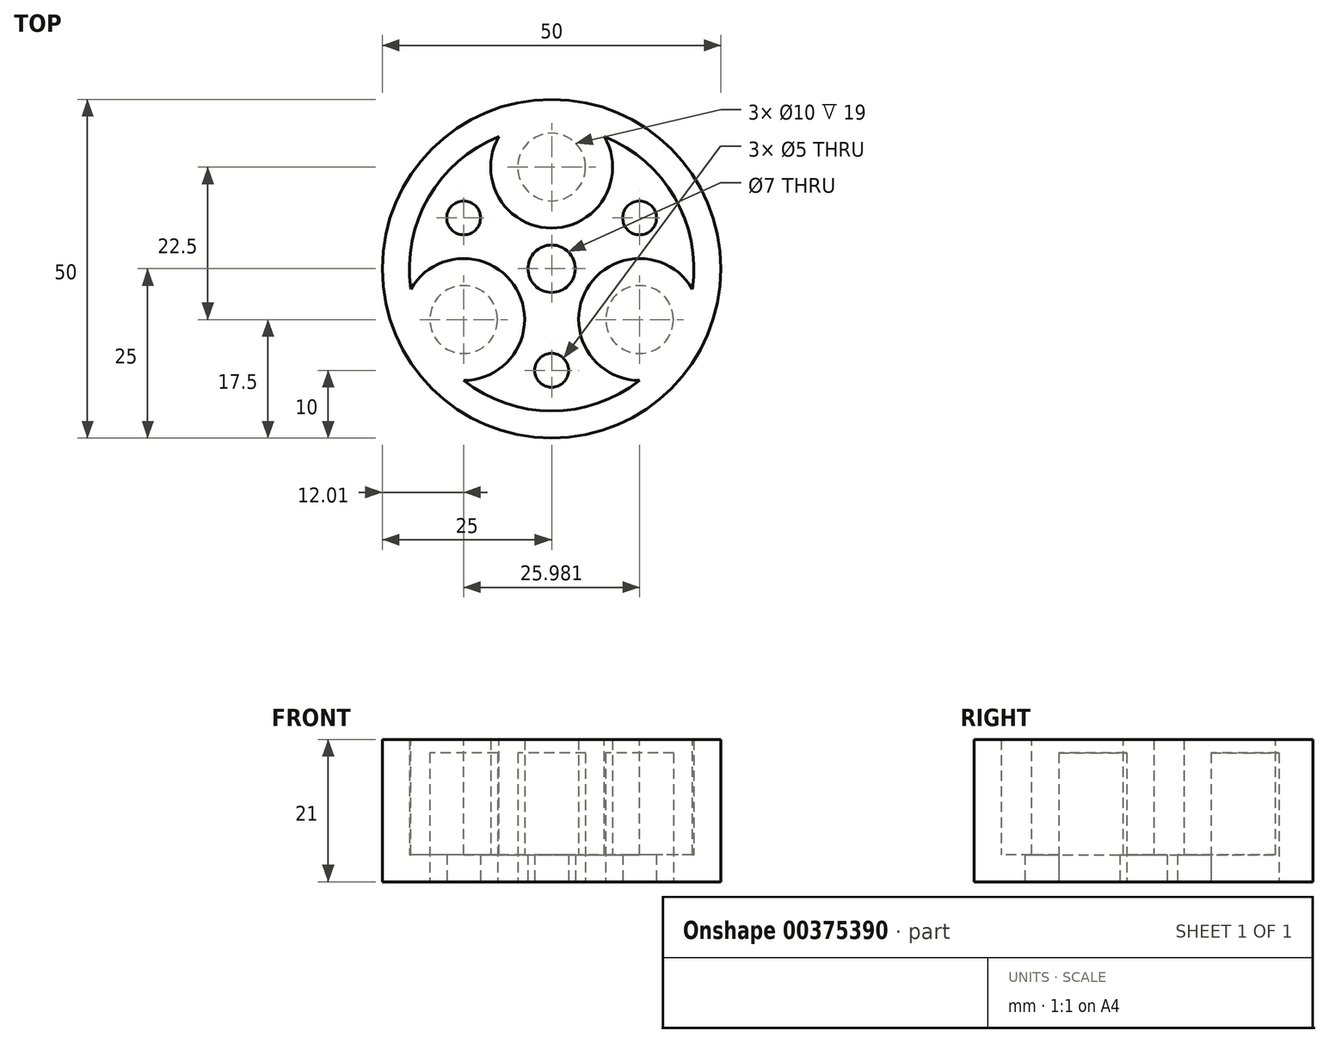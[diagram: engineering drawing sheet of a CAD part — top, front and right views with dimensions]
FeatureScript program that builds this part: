
annotation { "Feature Type Name" : "Feature", "Feature Type Description" : "" }
export const myFeature = defineFeature(function(context is Context, id is Id, definition is map)
    precondition{}
    {
        {
            var Q0;
            Q0=qCreatedBy(makeId("Top.planeOp"),FACE);
            var sketch = newSketch(context, id + "F0", { "sketchPlane" : qUnion([Q0])});
            skCircle(sketch, "E0", {"center": v(0, 0) * mm, "radius": 25 * mm});
            skCircle(sketch, "E1", {"center": v(0, 15) * mm, "radius": 5 * mm});
            skCircle(sketch, "E2", {"center": v(0, 0) * mm, "radius": 3.5 * mm});
            skCircle(sketch, "E3.1.0", {"center": v(-13, -7.5) * mm, "radius": 5 * mm});
            skCircle(sketch, "E3.2.0", {"center": v(13, -7.5) * mm, "radius": 5 * mm});
            skLineSegment(sketch, "E4", {"start": v(0, 15) * mm, "end": v(13, -7.5) * mm, "construction": true});
            skLineSegment(sketch, "E5", {"start": v(0, 0) * mm, "end": v(13, 7.5) * mm, "construction": true});
            skCircle(sketch, "E6", {"center": v(13, 7.5) * mm, "radius": 2.5 * mm});
            skCircle(sketch, "E7.1.0", {"center": v(-13, 7.5) * mm, "radius": 2.5 * mm});
            skCircle(sketch, "E7.2.0", {"center": v(0, -15) * mm, "radius": 2.5 * mm});
            skSolve(sketch);
        }
        {
            var Q0;
            Q0=qSketchRegion(id+"F0",true);
            var Q1;
            Q1=makeQuery(id+"F0.imprint","IMPRINT",FACE,{"disambiguationData":[TD([[makeQuery(id+"F0.imprint","IMPRINT",EDGE,{"derivedFrom":sQuery(id+"F0.wireOp",EDGE,"2f1edcd0-1068-4564-a11f-02244e7b30a9")}),1.0]])]});
            var Q2;
            Q2=makeQuery(id+"F0.imprint","IMPRINT",FACE,{"disambiguationData":[TD([[makeQuery(id+"F0.imprint","IMPRINT",EDGE,{"derivedFrom":sQuery(id+"F0.wireOp",EDGE,"E2")}),1.0]])]});
            var Q3;
            Q3=makeQuery(id+"F0.imprint","IMPRINT",FACE,{"disambiguationData":[TD([[makeQuery(id+"F0.imprint","IMPRINT",EDGE,{"derivedFrom":sQuery(id+"F0.wireOp",EDGE,"E7.1.0")}),1.0]])]});
            var Q4;
            Q4=makeQuery(id+"F0.imprint","IMPRINT",FACE,{"disambiguationData":[TD([[makeQuery(id+"F0.imprint","IMPRINT",EDGE,{"derivedFrom":sQuery(id+"F0.wireOp",EDGE,"E6")}),1.0]])]});
            var Q5;
            Q5=makeQuery(id+"F0.imprint","IMPRINT",FACE,{"disambiguationData":[TD([[makeQuery(id+"F0.imprint","IMPRINT",EDGE,{"derivedFrom":sQuery(id+"F0.wireOp",EDGE,"E7.2.0")}),1.0]])]});
            extrude(context, id + "F1", {"entities" : qUnion([Q0, Q1, Q2, Q3, Q4, Q5]), "depth" : 19 * mm});
        }
        {
            var Q0;
            Q0=makeQuery(id+"F1.opExtrude","CAP_FACE",FACE,{"disambiguationData":[OSD([sQuery(id+"F0.wireOp",EDGE,"E0"),sQuery(id+"F0.wireOp",EDGE,"E1"),sQuery(id+"F0.wireOp",EDGE,"15a5e05c-d03d-43cd-ad20-06248263a0d0.1.0"),sQuery(id+"F0.wireOp",EDGE,"15a5e05c-d03d-43cd-ad20-06248263a0d0.2.0"),sQuery(id+"F0.wireOp",EDGE,"15a5e05c-d03d-43cd-ad20-06248263a0d0.3.0")])],"isStart":false});
            shell(context, id + "F2", {"entities" : qUnion([Q0]), "thickness" : 4 * mm});
        }
        {
            var Q0;
            Q0=makeQuery(id+"F0.imprint","IMPRINT",FACE,{"disambiguationData":[TD([[makeQuery(id+"F0.imprint","IMPRINT",EDGE,{"derivedFrom":sQuery(id+"F0.wireOp",EDGE,"E7.1.0")}),1.0]])]});
            var Q1;
            Q1=makeQuery(id+"F0.imprint","IMPRINT",FACE,{"disambiguationData":[TD([[makeQuery(id+"F0.imprint","IMPRINT",EDGE,{"derivedFrom":sQuery(id+"F0.wireOp",EDGE,"E2")}),1.0]])]});
            var Q2;
            Q2=makeQuery(id+"F0.imprint","IMPRINT",FACE,{"disambiguationData":[TD([[makeQuery(id+"F0.imprint","IMPRINT",EDGE,{"derivedFrom":sQuery(id+"F0.wireOp",EDGE,"E6")}),1.0]])]});
            var Q3;
            Q3=makeQuery(id+"F0.imprint","IMPRINT",FACE,{"disambiguationData":[TD([[makeQuery(id+"F0.imprint","IMPRINT",EDGE,{"derivedFrom":sQuery(id+"F0.wireOp",EDGE,"E7.2.0")}),1.0]])]});
            extrude(context, id + "F3", {"entities" : qUnion([Q0, Q1, Q2, Q3]), "operationType" : NewBodyOperationType.REMOVE, "depth" : 25 * mm});
        }
        {
            var Q0;
            Q0=makeQuery(id+"F1.opExtrude","CAP_FACE",FACE,{"disambiguationData":[OSD([sQuery(id+"F0.wireOp",EDGE,"E0"),sQuery(id+"F0.wireOp",EDGE,"E1"),sQuery(id+"F0.wireOp",EDGE,"E3.1.0"),sQuery(id+"F0.wireOp",EDGE,"E3.2.0")])],"isStart":false});
            var sketch = newSketch(context, id + "F4", { "sketchPlane" : qUnion([Q0])});
            skCircle(sketch, "E8.0.0", {"center": v(0, 0) * mm, "radius": 25 * mm});
            skArc(sketch, "E9.0", {"start": v(-7.8, 19.5) * mm, "mid": v(-18.19, 10.5) * mm, "end": v(-20.78, -3) * mm});
            skArc(sketch, "E10.0", {"start": v(-7.8, 19.5) * mm, "mid": v(0, 6) * mm, "end": v(7.8, 19.5) * mm});
            skArc(sketch, "E11.0", {"start": v(20.78, -3) * mm, "mid": v(5.2, -3) * mm, "end": v(13, -16.5) * mm});
            skArc(sketch, "E12.0", {"start": v(20.78, -3) * mm, "mid": v(18.19, 10.5) * mm, "end": v(7.8, 19.5) * mm});
            skArc(sketch, "E13.0", {"start": v(-13, -16.5) * mm, "mid": v(0, -21) * mm, "end": v(13, -16.5) * mm});
            skArc(sketch, "E14.0", {"start": v(-13, -16.5) * mm, "mid": v(-5.2, -3) * mm, "end": v(-20.78, -3) * mm});
            skSolve(sketch);
        }
        {
            var Q0;
            Q0=qSketchRegion(id+"F4",true);
            extrude(context, id + "F5", {"entities" : qUnion([Q0]), "operationType" : NewBodyOperationType.ADD, "depth" : 2 * mm});
        }
    });
